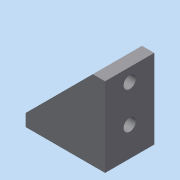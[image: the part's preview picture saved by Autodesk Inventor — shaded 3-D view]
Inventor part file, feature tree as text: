
AUTODESK INVENTOR PART (.ipt)
format: ipt  version: 2015 (Build 190159000, 159)  size: 129,536 bytes
history: native  units: in
note: dims shown in document units (in); Inventor stores cm internally (conversion verified against a paired STEP export)
features: sketch x6, extrude x5, hole x2
ambient origin geometry x8: Origin, YZ Plane, XZ Plane, XY Plane, X Axis, Y Axis, Z Axis, Center Point
bodies: Solid1 (feature_tree)
feature tree (13):
  extrude  "Extrusion1"  Depth=1.9685in
  sketch  "Sketch2"  dims[d2=0.7874in d3=0.0in d4=0.1969in]
  extrude  "Extrusion2"  Depth=0.1969in
  extrude  "Extrusion3"  Depth=0.1969in TaperAngle=0.0deg
  extrude  "Extrusion5"  Depth=0.5in
  hole  "Hole2"  [1 undecoded]
  hole  "Hole3"  [1 undecoded]
  extrude  "Extrusion6"  Depth=0.5906in
  sketch  "Sketch1"  dims[d0=1.9685in d1=1.9685in]
  sketch  "Sketch3"  dims[d5=0.1969in d6=0.2953in d7=0.0in]
  sketch  "Sketch5"  dims[d8=0.1969in d9=0.0in d12=0.5in]
  sketch  "Sketch6"  dims[d13=0.5in d14=0.0in d15=0.0in]
  sketch  "Sketch7"  dims[d28=0.3937in d29=0.3937in d30=0.5906in d31=0.4724in d32=0.1969in d33=0.75in d34=0.375in d35=0.25in d36=0.5635in d37=1.0in d38=0.8108in d39=0.5906in d40=0.3937in d41=0.3937in d42=0.4724in d43=0.1969in d44=0.75in d45=0.375in d46=0.25in d47=0.5635in d48=1.0in d49=0.8108in d50=1.0in d51=0.0in]
note: 2 required parameter values undecoded (feature->parameter linkage not recoverable at this tier; creation-order binding heuristic only, values carry confidence <= 0.55)
